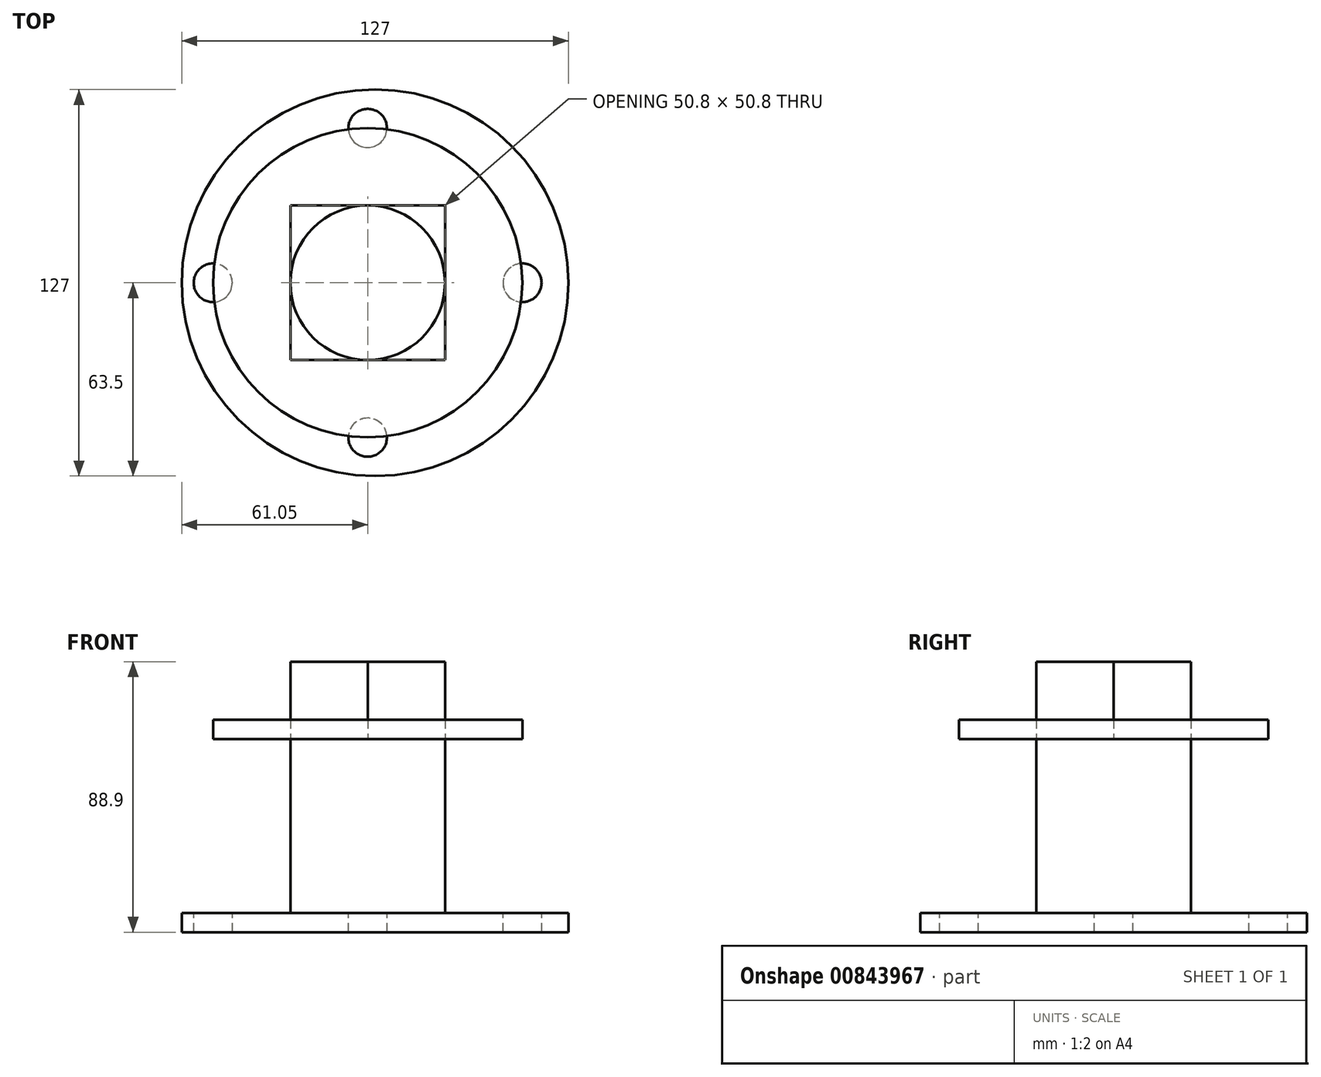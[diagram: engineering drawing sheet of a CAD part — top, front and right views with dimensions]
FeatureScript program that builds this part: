
annotation { "Feature Type Name" : "Feature", "Feature Type Description" : "" }
export const myFeature = defineFeature(function(context is Context, id is Id, definition is map)
    precondition{}
    {
        {
            var Q0;
            Q0=qCreatedBy(makeId("Top.planeOp"),FACE);
            var sketch = newSketch(context, id + "F0", { "sketchPlane" : qUnion([Q0])});
            skCircle(sketch, "E0", {"center": v(2.45, 0) * mm, "radius": 63.5 * mm});
            skSolve(sketch);
        }
        {
            var Q0;
            Q0=makeQuery(id+"F0.imprint","IMPRINT",FACE,{"disambiguationData":[TD([[makeQuery(id+"F0.imprint","IMPRINT",EDGE,{"derivedFrom":sQuery(id+"F0.wireOp",EDGE,"E0")}),1.0]])]});
            extrude(context, id + "F1", {"entities" : qUnion([Q0]), "depth" : 6.35 * mm, "offsetDistance" : 25.4 * mm});
        }
        {
            var Q0;
            Q0=makeQuery(id+"F1.opExtrude","CAP_FACE",FACE,{"disambiguationData":[OSD([sQuery(id+"F0.wireOp",EDGE,"E0")])],"isStart":false});
            var sketch = newSketch(context, id + "F2", { "sketchPlane" : qUnion([Q0])});
            skCircle(sketch, "E1", {"center": v(0, 0) * mm, "radius": 25.4 * mm});
            skSolve(sketch);
        }
        {
            var Q0;
            Q0=makeQuery(id+"F2.imprint","IMPRINT",FACE,{"disambiguationData":[TD([[makeQuery(id+"F2.imprint","IMPRINT",EDGE,{"derivedFrom":sQuery(id+"F2.wireOp",EDGE,"E1")}),1.0]])]});
            extrude(context, id + "F3", {"entities" : qUnion([Q0]), "operationType" : NewBodyOperationType.ADD, "depth" : 57.15 * mm, "offsetDistance" : 25.4 * mm});
        }
        {
            var Q0;
            Q0=makeQuery(id+"F1.opExtrude","CAP_FACE",FACE,{"disambiguationData":[OSD([sQuery(id+"F0.wireOp",EDGE,"E0")])],"isStart":false});
            var sketch = newSketch(context, id + "F4", { "sketchPlane" : qUnion([Q0])});
            skCircle(sketch, "E2", {"center": v(0, 50.8) * mm, "radius": 6.35 * mm});
            skSolve(sketch);
        }
        {
            var Q0;
            Q0=makeQuery(id+"F4.imprint","IMPRINT",FACE,{"disambiguationData":[TD([[makeQuery(id+"F4.imprint","IMPRINT",EDGE,{"derivedFrom":sQuery(id+"F4.wireOp",EDGE,"E2")}),1.0]])]});
            extrude(context, id + "F5", {"entities" : qUnion([Q0]), "operationType" : NewBodyOperationType.REMOVE, "oppositeDirection" : true, "depth" : 25.4 * mm, "offsetDistance" : 25.4 * mm});
        }
        {
            var Q0;
            Q0=makeQuery(id+"F1.opExtrude","CAP_FACE",FACE,{"disambiguationData":[OSD([sQuery(id+"F0.wireOp",EDGE,"E0")])],"isStart":false});
            var sketch = newSketch(context, id + "F6", { "sketchPlane" : qUnion([Q0])});
            skCircle(sketch, "E3", {"center": v(-50.8, 0) * mm, "radius": 6.35 * mm});
            skSolve(sketch);
        }
        {
            var Q0;
            Q0=makeQuery(id+"F6.imprint","IMPRINT",FACE,{"disambiguationData":[TD([[makeQuery(id+"F6.imprint","IMPRINT",EDGE,{"derivedFrom":sQuery(id+"F6.wireOp",EDGE,"E3")}),1.0]])]});
            var Q1;
            Q1=sQuery(id+"F6.wireOp",EDGE,"E3");
            extrude(context, id + "F7", {"entities" : qUnion([Q0]), "operationType" : NewBodyOperationType.REMOVE, "surfaceEntities" : qUnion([Q1]), "oppositeDirection" : true, "depth" : 25.4 * mm, "offsetDistance" : 25.4 * mm});
        }
        {
            var Q0;
            Q0=makeQuery(id+"F1.opExtrude","CAP_FACE",FACE,{"disambiguationData":[OSD([sQuery(id+"F0.wireOp",EDGE,"E0")])],"isStart":false});
            var sketch = newSketch(context, id + "F8", { "sketchPlane" : qUnion([Q0])});
            skCircle(sketch, "E4", {"center": v(0, -50.8) * mm, "radius": 6.35 * mm});
            skSolve(sketch);
        }
        {
            var Q0;
            Q0=makeQuery(id+"F8.imprint","IMPRINT",FACE,{"disambiguationData":[TD([[makeQuery(id+"F8.imprint","IMPRINT",EDGE,{"derivedFrom":sQuery(id+"F8.wireOp",EDGE,"E4")}),1.0]])]});
            extrude(context, id + "F9", {"entities" : qUnion([Q0]), "operationType" : NewBodyOperationType.REMOVE, "oppositeDirection" : true, "depth" : 25.4 * mm, "offsetDistance" : 25.4 * mm});
        }
        {
            var Q0;
            Q0=makeQuery(id+"F1.opExtrude","CAP_FACE",FACE,{"disambiguationData":[OSD([sQuery(id+"F0.wireOp",EDGE,"E0")])],"isStart":false});
            var sketch = newSketch(context, id + "F10", { "sketchPlane" : qUnion([Q0])});
            skCircle(sketch, "E5", {"center": v(50.8, 0) * mm, "radius": 6.35 * mm});
            skSolve(sketch);
        }
        {
            var Q0;
            Q0=makeQuery(id+"F10.imprint","IMPRINT",FACE,{"disambiguationData":[TD([[makeQuery(id+"F10.imprint","IMPRINT",EDGE,{"derivedFrom":sQuery(id+"F10.wireOp",EDGE,"E5")}),1.0]])]});
            extrude(context, id + "F11", {"entities" : qUnion([Q0]), "operationType" : NewBodyOperationType.REMOVE, "oppositeDirection" : true, "depth" : 25.4 * mm, "offsetDistance" : 25.4 * mm});
        }
        {
            var Q0;
            Q0=makeQuery(id+"F3.opExtrude","CAP_FACE",FACE,{"disambiguationData":[OSD([sQuery(id+"F2.wireOp",EDGE,"E1")])],"isStart":false});
            var sketch = newSketch(context, id + "F12", { "sketchPlane" : qUnion([Q0])});
            skCircle(sketch, "E6", {"center": v(0, 0) * mm, "radius": 50.8 * mm});
            skSolve(sketch);
        }
        {
            var Q0;
            Q0=makeQuery(id+"F12.imprint","IMPRINT",FACE,{"disambiguationData":[TD([[makeQuery(id+"F12.imprint","IMPRINT",EDGE,{"derivedFrom":sQuery(id+"F12.wireOp",EDGE,"E6")}),1.0]])]});
            extrude(context, id + "F13", {"entities" : qUnion([Q0]), "depth" : 6.35 * mm, "offsetDistance" : 25.4 * mm});
        }
        {
            var Q0;
            Q0=makeQuery(id+"F3.opExtrude","CAP_FACE",FACE,{"disambiguationData":[OSD([sQuery(id+"F2.wireOp",EDGE,"E1")])],"isStart":false});
            var sketch = newSketch(context, id + "F14", { "sketchPlane" : qUnion([Q0])});
            skLineSegment(sketch, "E7.bottom", {"start": v(-25.4, 25.4) * mm, "end": v(25.4, 25.4) * mm});
            skLineSegment(sketch, "E7.top", {"start": v(-25.4, -25.4) * mm, "end": v(25.4, -25.4) * mm});
            skLineSegment(sketch, "E7.left", {"start": v(-25.4, 25.4) * mm, "end": v(-25.4, -25.4) * mm});
            skLineSegment(sketch, "E7.right", {"start": v(25.4, 25.4) * mm, "end": v(25.4, -25.4) * mm});
            skPoint(sketch, "E7.middle", {"position": v(0, 0) * mm});
            skSolve(sketch);
        }
        {
            var Q0;
            {var subQ0=sQuery(id+"F14.wireOp",EDGE,"E7.left");var subQ1=sQuery(id+"F14.wireOp",EDGE,"E7.bottom");var subQ2=makeQuery(id+"F14.imprint","INTERSECT",VERTEX,{"derivedFrom":[subQ1,subQ0]});Q0=makeQuery(id+"F14.imprint","IMPRINT",FACE,{"disambiguationData":[TD([[makeQuery(id+"F14.imprint","IMPRINT",EDGE,{"disambiguationData":[TD([[subQ2,-1.0]])],"derivedFrom":subQ1}),-1.0]])]});}
            var Q1;
            {var subQ0=sQuery(id+"F14.wireOp",EDGE,"E7.right");var subQ1=sQuery(id+"F14.wireOp",EDGE,"E7.bottom");var subQ2=makeQuery(id+"F14.imprint","INTERSECT",VERTEX,{"derivedFrom":[subQ1,subQ0]});Q1=makeQuery(id+"F14.imprint","IMPRINT",FACE,{"disambiguationData":[TD([[makeQuery(id+"F14.imprint","IMPRINT",EDGE,{"disambiguationData":[TD([[subQ2,1.0]])],"derivedFrom":subQ1}),-1.0]])]});}
            var Q2;
            {var subQ0=sQuery(id+"F14.wireOp",EDGE,"E7.left");var subQ1=sQuery(id+"F14.wireOp",EDGE,"E7.top");var subQ2=makeQuery(id+"F14.imprint","INTERSECT",VERTEX,{"derivedFrom":[subQ1,subQ0]});Q2=makeQuery(id+"F14.imprint","IMPRINT",FACE,{"disambiguationData":[TD([[makeQuery(id+"F14.imprint","IMPRINT",EDGE,{"disambiguationData":[TD([[subQ2,-1.0]])],"derivedFrom":subQ1}),1.0]])]});}
            var Q3;
            {var subQ0=sQuery(id+"F14.wireOp",EDGE,"E7.right");var subQ1=sQuery(id+"F14.wireOp",EDGE,"E7.top");var subQ2=makeQuery(id+"F14.imprint","INTERSECT",VERTEX,{"derivedFrom":[subQ1,subQ0]});Q3=makeQuery(id+"F14.imprint","IMPRINT",FACE,{"disambiguationData":[TD([[makeQuery(id+"F14.imprint","IMPRINT",EDGE,{"disambiguationData":[TD([[subQ2,1.0]])],"derivedFrom":subQ1}),1.0]])]});}
            extrude(context, id + "F15", {"entities" : qUnion([Q0, Q1, Q2, Q3]), "operationType" : NewBodyOperationType.ADD, "depth" : 25.4 * mm, "offsetDistance" : 25.4 * mm});
        }
        {
            var Q0;
            Q0=qCreatedBy(makeId("Top.planeOp"),FACE);
            var sketch = newSketch(context, id + "F16", { "sketchPlane" : qUnion([Q0])});
            skLineSegment(sketch, "E8.bottom", {"start": v(-25.4, -25.4) * mm, "end": v(25.4, -25.4) * mm});
            skLineSegment(sketch, "E8.top", {"start": v(-25.4, 25.4) * mm, "end": v(25.4, 25.4) * mm});
            skLineSegment(sketch, "E8.left", {"start": v(-25.4, -25.4) * mm, "end": v(-25.4, 25.4) * mm});
            skLineSegment(sketch, "E8.right", {"start": v(25.4, -25.4) * mm, "end": v(25.4, 25.4) * mm});
            skPoint(sketch, "E8.middle", {"position": v(0, 0) * mm});
            skSolve(sketch);
        }
        {
            var Q0;
            Q0=makeQuery(id+"F16.imprint","IMPRINT",FACE,{"disambiguationData":[TD([[makeQuery(id+"F16.imprint","IMPRINT",EDGE,{"derivedFrom":sQuery(id+"F16.wireOp",EDGE,"E8.bottom")}),1.0]])]});
            extrude(context, id + "F17", {"entities" : qUnion([Q0]), "operationType" : NewBodyOperationType.REMOVE, "oppositeDirection" : true, "depth" : 127 * mm, "offsetDistance" : 25.4 * mm});
        }
    });
